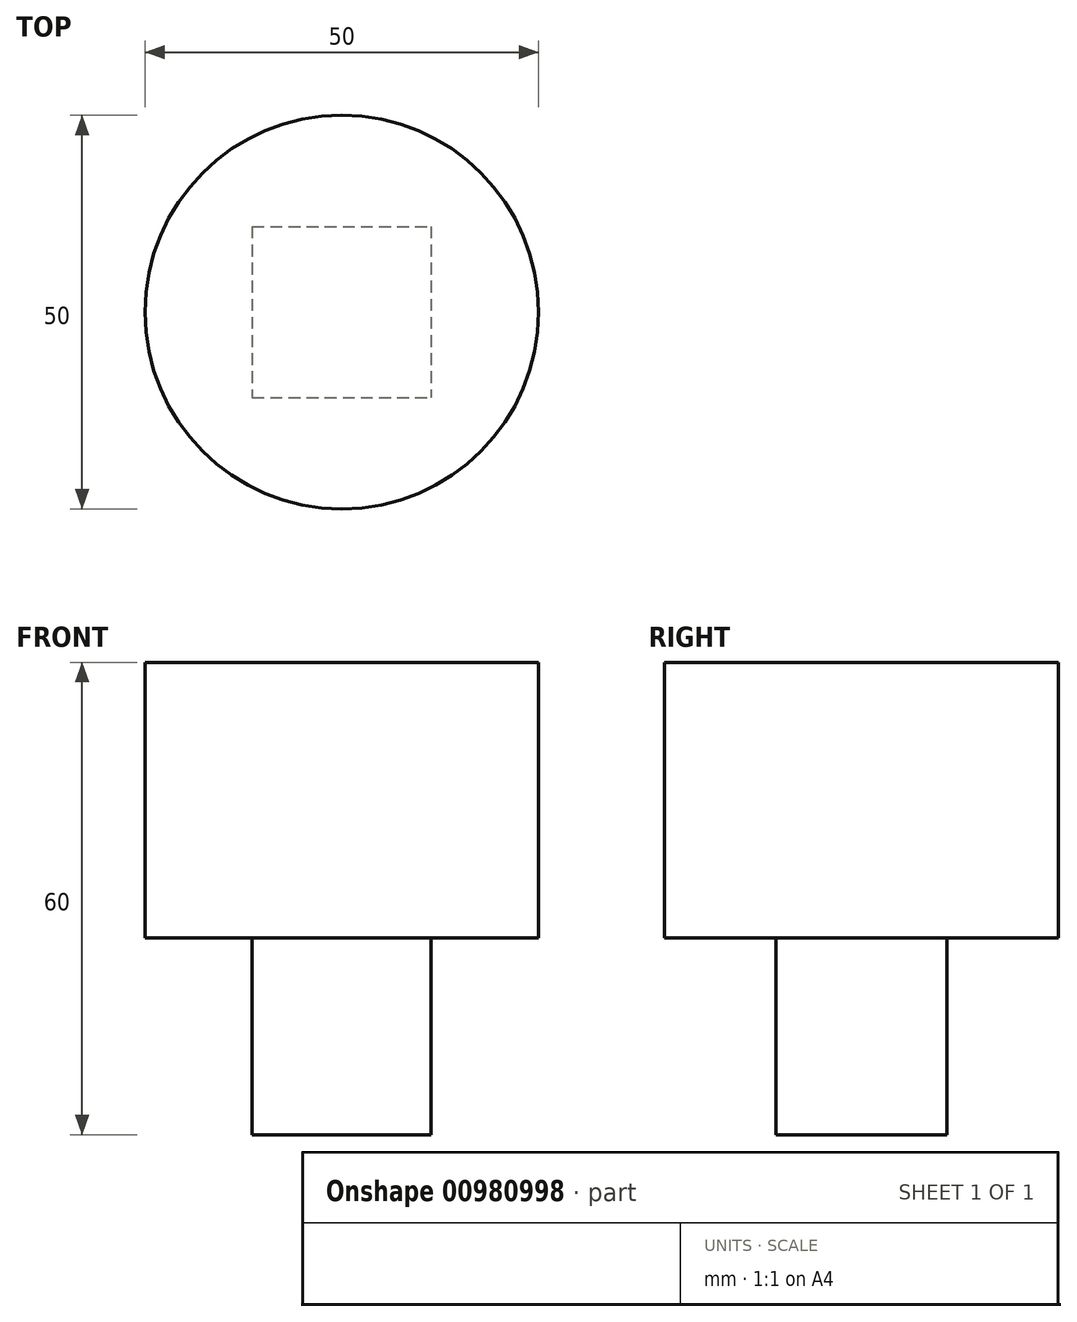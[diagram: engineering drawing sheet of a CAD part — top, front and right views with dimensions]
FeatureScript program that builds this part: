
annotation { "Feature Type Name" : "Feature", "Feature Type Description" : "" }
export const myFeature = defineFeature(function(context is Context, id is Id, definition is map)
    precondition{}
    {
        {
            var Q0;
            Q0=qCreatedBy(makeId("Top.planeOp"),FACE);
            var sketch = newSketch(context, id + "F0", { "sketchPlane" : qUnion([Q0])});
            skCircle(sketch, "E0", {"center": v(0, 0) * mm, "radius": 25 * mm});
            skCircle(sketch, "E1", {"center": v(0, 50) * mm, "radius": 17.5 * mm});
            skSolve(sketch);
        }
        {
            var Q0;
            Q0=makeQuery(id+"F0.imprint","IMPRINT",FACE,{"disambiguationData":[TD([[makeQuery(id+"F0.imprint","IMPRINT",EDGE,{"derivedFrom":sQuery(id+"F0.wireOp",EDGE,"E0")}),1.0]])]});
            extrude(context, id + "F1", {"entities" : qUnion([Q0]), "oppositeDirection" : true, "depth" : 35 * mm, "offsetDistance" : 25 * mm, "symmetric" : true});
        }
        {
            var Q0;
            Q0=makeQuery(id+"F1.opExtrude","CAP_FACE",FACE,{"disambiguationData":[OSD([sQuery(id+"F0.wireOp",EDGE,"E0")])],"isStart":false});
            var sketch = newSketch(context, id + "F2", { "sketchPlane" : qUnion([Q0])});
            skLineSegment(sketch, "E2.bottom", {"start": v(-11.37, -10.88) * mm, "end": v(11.37, -10.88) * mm});
            skLineSegment(sketch, "E2.top", {"start": v(-11.37, 10.88) * mm, "end": v(11.37, 10.88) * mm});
            skLineSegment(sketch, "E2.left", {"start": v(-11.37, -10.88) * mm, "end": v(-11.37, 10.88) * mm});
            skLineSegment(sketch, "E2.right", {"start": v(11.37, -10.88) * mm, "end": v(11.37, 10.88) * mm});
            skPoint(sketch, "E2.middle", {"position": v(0, 0) * mm});
            skSolve(sketch);
        }
        {
            var Q0;
            Q0=makeQuery(id+"F2.imprint","IMPRINT",FACE,{"disambiguationData":[TD([[makeQuery(id+"F2.imprint","IMPRINT",EDGE,{"derivedFrom":sQuery(id+"F2.wireOp",EDGE,"E2.bottom")}),1.0]])]});
            extrude(context, id + "F3", {"entities" : qUnion([Q0]), "operationType" : NewBodyOperationType.ADD, "depth" : 25 * mm, "offsetDistance" : 25 * mm});
        }
    });
